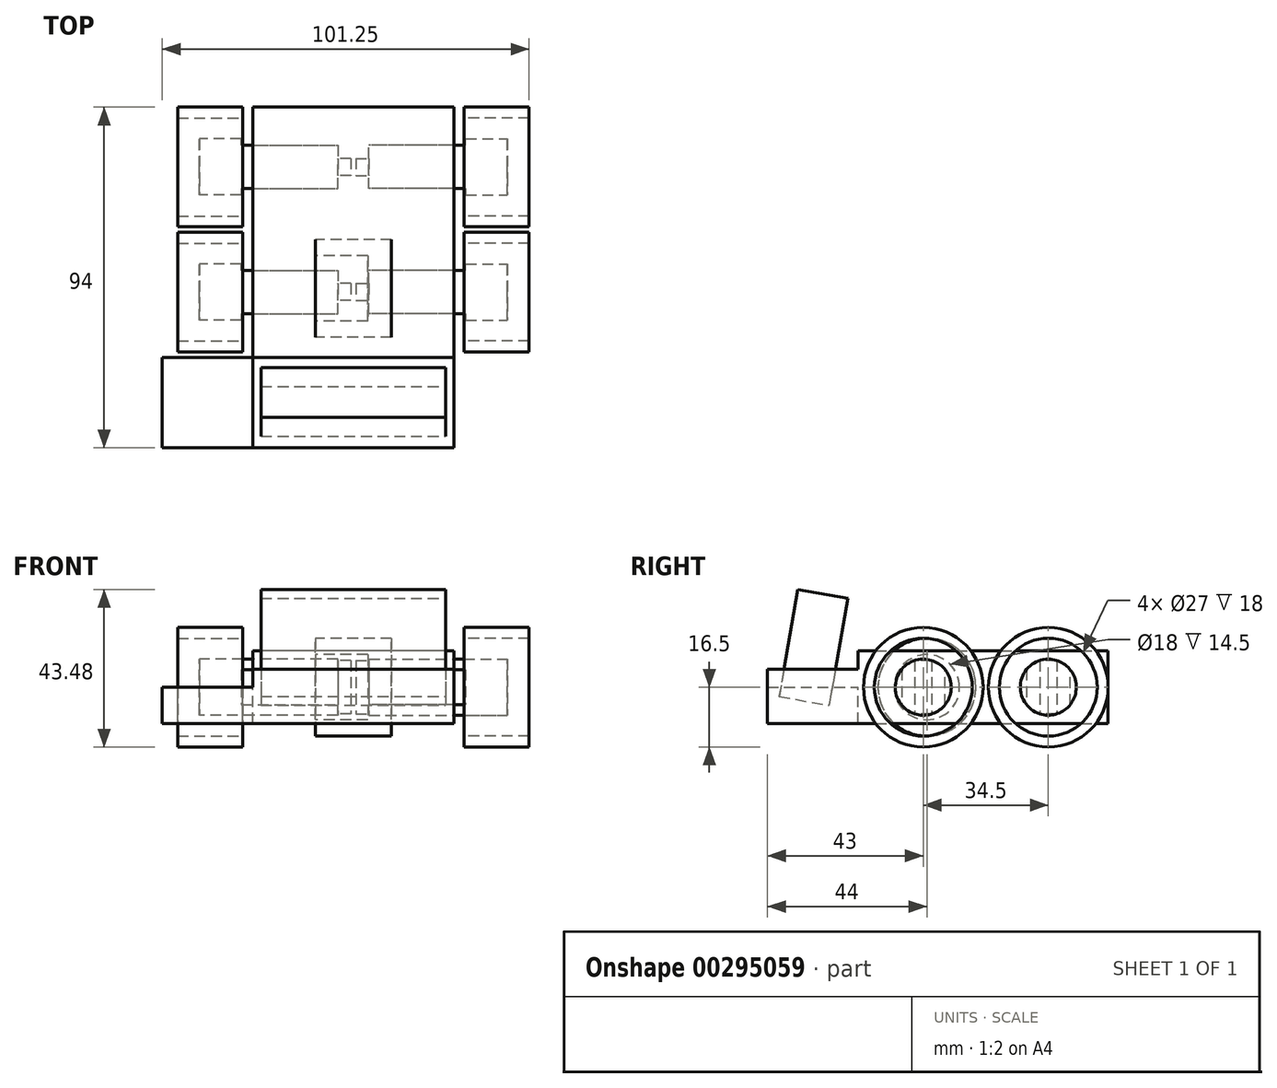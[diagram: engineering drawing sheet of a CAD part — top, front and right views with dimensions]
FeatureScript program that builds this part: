
annotation { "Feature Type Name" : "Feature", "Feature Type Description" : "" }
export const myFeature = defineFeature(function(context is Context, id is Id, definition is map)
    precondition{}
    {
        {
            assignVariable(context, id + "F0", {"name" : "GapMid", "anyValue" : 1.5 * mm});
        }
        {
            var Q0;
            Q0=qCreatedBy(makeId("Top.planeOp"),FACE);
            var sketch = newSketch(context, id + "F1", { "sketchPlane" : qUnion([Q0])});
            skLineSegment(sketch, "E0.bottom", {"start": v(-50, 50) * mm, "end": v(50, 50) * mm, "construction": true});
            skLineSegment(sketch, "E0.top", {"start": v(-50, -50) * mm, "end": v(50, -50) * mm, "construction": true});
            skLineSegment(sketch, "E0.left", {"start": v(-50, 50) * mm, "end": v(-50, -50) * mm, "construction": true});
            skLineSegment(sketch, "E0.right", {"start": v(50, 50) * mm, "end": v(50, -50) * mm, "construction": true});
            skLineSegment(sketch, "E1", {"start": v(0, 0) * mm, "end": v(39.5, 33.5) * mm, "construction": true});
            skSolve(sketch);
        }
        {
            var Q0;
            Q0=qCreatedBy(makeId("Right.planeOp"),FACE);
            var sketch = newSketch(context, id + "F2", { "sketchPlane" : qUnion([Q0])});
            skCircle(sketch, "E2", {"center": v(0, 0) * mm, "radius": 13.5 * mm});
            skCircle(sketch, "E3", {"center": v(0, 0) * mm, "radius": 16.5 * mm});
            skSolve(sketch);
        }
        {
            var Q0;
            Q0=makeQuery(id+"F2.imprint","IMPRINT",FACE,{"disambiguationData":[TD([[makeQuery(id+"F2.imprint","IMPRINT",EDGE,{"derivedFrom":sQuery(id+"F2.wireOp",EDGE,"E2")}),-1.0]])]});
            extrude(context, id + "F3", {"entities" : qUnion([Q0]), "endBound" : BoundingType.SYMMETRIC, "depth" : 18 * mm});
        }
        {
            var Q0;
            Q0=makeQuery(id+"F2.imprint","IMPRINT",FACE,{"disambiguationData":[TD([[makeQuery(id+"F2.imprint","IMPRINT",EDGE,{"derivedFrom":sQuery(id+"F2.wireOp",EDGE,"E2")}),1.0]])]});
            extrude(context, id + "F4", {"entities" : qUnion([Q0]), "endBound" : BoundingType.SYMMETRIC, "depth" : 21 * mm});
        }
        {
            var Q0;
            Q0=makeQuery(id+"F4.opExtrude","CAP_FACE",FACE,{"disambiguationData":[OSD([sQuery(id+"F2.wireOp",EDGE,"E2")])],"isStart":true});
            var sketch = newSketch(context, id + "F5", { "sketchPlane" : qUnion([Q0])});
            skCircle(sketch, "E4", {"center": v(0, 0) * mm, "radius": 9 * mm});
            skSolve(sketch);
        }
        {
            var Q0;
            Q0=makeQuery(id+"F5.imprint","IMPRINT",FACE,{"disambiguationData":[TD([[makeQuery(id+"F5.imprint","IMPRINT",EDGE,{"derivedFrom":sQuery(id+"F5.wireOp",EDGE,"E4")}),1.0]])]});
            var Q1;
            Q1=sQuery(id+"F5.wireOp",EDGE,"E4");
            extrude(context, id + "F6", {"entities" : qUnion([Q0]), "operationType" : NewBodyOperationType.REMOVE, "surfaceEntities" : qUnion([Q1]), "oppositeDirection" : true, "depth" : 14.5 * mm});
        }
        {
            var Q0;
            Q0=makeQuery(id+"F6.boolean.opBoolean","COPY",FACE,{"derivedFrom":makeQuery(id+"F6.opExtrude","CAP_FACE",FACE,{"disambiguationData":[OSD([sQuery(id+"F5.wireOp",EDGE,"E4")])],"isStart":false})});
            cPlane(context, id + "F7", {"entities" : qUnion([Q0]), "cplaneType" : CPlaneType.OFFSET, "offset" : 1 * mm, "width" : 150 * mm, "height" : 150 * mm});
        }
        {
            var Q0;
            Q0=qCreatedBy(id+"F7.planeOp",FACE);
            var sketch = newSketch(context, id + "F8", { "sketchPlane" : qUnion([Q0])});
            skCircle(sketch, "E5", {"center": v(0, 0) * mm, "radius": 7.73 * mm});
            skSolve(sketch);
        }
        {
            var Q0;
            Q0=makeQuery(id+"F8.imprint","IMPRINT",FACE,{"disambiguationData":[TD([[makeQuery(id+"F8.imprint","IMPRINT",EDGE,{"derivedFrom":sQuery(id+"F8.wireOp",EDGE,"E5")}),1.0]])]});
            extrude(context, id + "F9", {"entities" : qUnion([Q0]), "depth" : 38.22 * mm});
        }
        {
            var Q0;
            Q0=makeQuery(id+"F9.opExtrude","CAP_FACE",FACE,{"disambiguationData":[OSD([sQuery(id+"F8.wireOp",EDGE,"E5")])],"isStart":false});
            var sketch = newSketch(context, id + "F10", { "sketchPlane" : qUnion([Q0])});
            skLineSegment(sketch, "E6", {"start": v(-6, 0) * mm, "end": v(6, 0) * mm, "construction": true});
            skLineSegment(sketch, "E7", {"start": v(-6, -4.87) * mm, "end": v(-6, 4.87) * mm});
            skLineSegment(sketch, "E8", {"start": v(6, 4.87) * mm, "end": v(6, -4.87) * mm});
            skSolve(sketch);
        }
        {
            var Q0;
            {var subQ0=sQuery(id+"F10.wireOp",EDGE,"E7");Q0=makeQuery(id+"F10.imprint","IMPRINT",FACE,{"disambiguationData":[TD([[makeQuery(id+"F10.imprint","IMPRINT",EDGE,{"derivedFrom":subQ0}),1.0]])]});}
            var Q1;
            {var subQ0=sQuery(id+"F10.wireOp",EDGE,"E8");Q1=makeQuery(id+"F10.imprint","IMPRINT",FACE,{"disambiguationData":[TD([[makeQuery(id+"F10.imprint","IMPRINT",EDGE,{"derivedFrom":subQ0}),1.0]])]});}
            extrude(context, id + "F11", {"entities" : qUnion([Q0, Q1]), "operationType" : NewBodyOperationType.REMOVE, "oppositeDirection" : true, "depth" : 26.7 * mm});
        }
        {
            var Q0;
            Q0=makeQuery(id+"F9.opExtrude","CAP_FACE",FACE,{"disambiguationData":[OSD([sQuery(id+"F8.wireOp",EDGE,"E5")])],"isStart":false});
            var sketch = newSketch(context, id + "F12", { "sketchPlane" : qUnion([Q0])});
            skLineSegment(sketch, "E9", {"start": v(-2.35, 7.36) * mm, "end": v(2.35, 7.36) * mm});
            skLineSegment(sketch, "E10", {"start": v(-2.35, -7.36) * mm, "end": v(2.35, -7.36) * mm});
            skLineSegment(sketch, "E11", {"start": v(-2.35, 7.36) * mm, "end": v(-2.35, -7.36) * mm});
            skLineSegment(sketch, "E12", {"start": v(2.35, 7.36) * mm, "end": v(2.35, -7.36) * mm});
            skSolve(sketch);
        }
        {
            var Q0;
            Q0=makeQuery(id+"F12.imprint","IMPRINT",FACE,{"disambiguationData":[TD([[makeQuery(id+"F12.imprint","IMPRINT",EDGE,{"derivedFrom":sQuery(id+"F12.wireOp",EDGE,"E9")}),-1.0]])]});
            extrude(context, id + "F13", {"entities" : qUnion([Q0]), "operationType" : NewBodyOperationType.ADD, "depth" : 3.6 * mm});
        }
        {
            var Q0;
            Q0=makeQuery(id+"F3.opExtrude","SWEPT_BODY",BODY,{"disambiguationData":[OSD([sQuery(id+"F2.wireOp",EDGE,"E2"),sQuery(id+"F2.wireOp",EDGE,"E3")])]});
            var Q1;
            Q1=makeQuery(id+"F9.opExtrude","SWEPT_BODY",BODY,{"disambiguationData":[OSD([sQuery(id+"F8.wireOp",EDGE,"E5")])]});
            var Q2;
            Q2=sQuery(id+"F1.wireOp",EDGE,"E1");
            transform(context, id + "F14", {"entities" : qUnion([Q0, Q1]), "transformType" : TransformType.TRANSLATION_ENTITY, "oppositeDirectionEntity" : false, "transformLine" : qUnion([Q2]), "makeCopy" : false});
        }
        {
            var Q0;
            Q0=makeQuery(id+"F3.opExtrude","SWEPT_BODY",BODY,{"disambiguationData":[OSD([sQuery(id+"F2.wireOp",EDGE,"E2"),sQuery(id+"F2.wireOp",EDGE,"E3")])]});
            var Q1;
            Q1=makeQuery(id+"F9.opExtrude","SWEPT_BODY",BODY,{"disambiguationData":[OSD([sQuery(id+"F8.wireOp",EDGE,"E5")])]});
            var Q2;
            Q2=qCreatedBy(makeId("Right.planeOp"),FACE);
            mirror(context, id + "F15", {"entities" : qUnion([Q0, Q1]), "mirrorPlane" : qUnion([Q2])});
        }
        {
            var Q0;
            Q0=makeQuery(id+"F15.opPattern","COPY",BODY,{"derivedFrom":makeQuery(id+"F3.opExtrude","SWEPT_BODY",BODY,{"disambiguationData":[OSD([sQuery(id+"F2.wireOp",EDGE,"E2"),sQuery(id+"F2.wireOp",EDGE,"E3")])]}),"instanceName":"1"});
            var Q1;
            Q1=makeQuery(id+"F3.opExtrude","SWEPT_BODY",BODY,{"disambiguationData":[OSD([sQuery(id+"F2.wireOp",EDGE,"E2"),sQuery(id+"F2.wireOp",EDGE,"E3")])]});
            var Q2;
            Q2=makeQuery(id+"F9.opExtrude","SWEPT_BODY",BODY,{"disambiguationData":[OSD([sQuery(id+"F8.wireOp",EDGE,"E5")])]});
            var Q3;
            Q3=makeQuery(id+"F15.opPattern","COPY",BODY,{"derivedFrom":makeQuery(id+"F9.opExtrude","SWEPT_BODY",BODY,{"disambiguationData":[OSD([sQuery(id+"F8.wireOp",EDGE,"E5")])]}),"instanceName":"1"});
            var Q4;
            Q4=makeQuery(id+"F15.opPattern","COPY",FACE,{"derivedFrom":makeQuery(id+"F11.boolean.opBoolean","COPY",FACE,{"derivedFrom":makeQuery(id+"F11.opExtrude","SWEPT_FACE",FACE,{"disambiguationData":[OSD([sQuery(id+"F10.wireOp",EDGE,"E8")])]})}),"instanceName":"1"});
            transform(context, id + "F16", {"entities" : qUnion([Q0, Q1, Q2, Q3]), "transformType" : TransformType.TRANSLATION_DISTANCE, "transformDirection" : qUnion([Q4]), "distance" : getVariable(context, 'GapMid') + 33 * mm, "makeCopy" : true});
        }
        {
            var Q0;
            Q0=makeQuery(id+"F16.opPattern","COPY",FACE,{"derivedFrom":makeQuery(id+"F15.opPattern","COPY",FACE,{"derivedFrom":makeQuery(id+"F4.opExtrude","CAP_FACE",FACE,{"disambiguationData":[OSD([sQuery(id+"F2.wireOp",EDGE,"E2")])],"isStart":false}),"instanceName":"1"}),"instanceName":"1"});
            var sketch = newSketch(context, id + "F17", { "sketchPlane" : qUnion([Q0])});
            skPoint(sketch, "E13", {"position": v(1, 0) * mm});
            skLineSegment(sketch, "E14", {"start": v(1, -5.4) * mm, "end": v(1, 5.4) * mm});
            skSolve(sketch);
        }
        {
            var Q0;
            Q0=qCreatedBy(makeId("Top.planeOp"),FACE);
            var sketch = newSketch(context, id + "F18", { "sketchPlane" : qUnion([Q0])});
            skLineSegment(sketch, "E15.bottom", {"start": v(27.75, -19) * mm, "end": v(-27.75, -19) * mm});
            skLineSegment(sketch, "E15.top", {"start": v(27.75, 50) * mm, "end": v(-27.75, 50) * mm});
            skLineSegment(sketch, "E15.left", {"start": v(27.75, -19) * mm, "end": v(27.75, 50) * mm});
            skLineSegment(sketch, "E15.right", {"start": v(-27.75, -19) * mm, "end": v(-27.75, 50) * mm});
            skSolve(sketch);
        }
        {
            var Q0;
            Q0=makeQuery(id+"F18.imprint","IMPRINT",FACE,{"disambiguationData":[TD([[makeQuery(id+"F18.imprint","IMPRINT",EDGE,{"derivedFrom":sQuery(id+"F18.wireOp",EDGE,"E15.bottom")}),-1.0]])]});
            extrude(context, id + "F19", {"entities" : qUnion([Q0]), "oppositeDirection" : true, "depth" : 10 * mm});
        }
        {
            var Q0;
            Q0=makeQuery(id+"F18.imprint","IMPRINT",FACE,{"disambiguationData":[TD([[makeQuery(id+"F18.imprint","IMPRINT",EDGE,{"derivedFrom":sQuery(id+"F18.wireOp",EDGE,"E15.bottom")}),-1.0]])]});
            var sketch = newSketch(context, id + "F20", { "sketchPlane" : qUnion([Q0])});
            skLineSegment(sketch, "E16.bottom", {"start": v(-25.5, 15) * mm, "end": v(25.5, 15) * mm});
            skLineSegment(sketch, "E16.top", {"start": v(-25.5, -15) * mm, "end": v(25.5, -15) * mm});
            skLineSegment(sketch, "E16.left", {"start": v(-25.5, 15) * mm, "end": v(-25.5, -15) * mm});
            skLineSegment(sketch, "E16.right", {"start": v(25.5, 15) * mm, "end": v(25.5, -15) * mm});
            skLineSegment(sketch, "E17", {"start": v(0, -15) * mm, "end": v(0, 15) * mm, "construction": true});
            skSolve(sketch);
        }
        {
            var Q0;
            Q0 = qSketchRegion(id + "F20", true);
            extrude(context, id + "F21", {"entities" : qUnion([Q0]), "depth" : 14 * mm});
        }
        {
            var Q0;
            Q0=makeQuery(id+"F21.opExtrude","SWEPT_BODY",BODY,{"disambiguationData":[OSD([sQuery(id+"F20.wireOp",EDGE,"E16.bottom"),sQuery(id+"F20.wireOp",EDGE,"E16.top"),sQuery(id+"F20.wireOp",EDGE,"E16.left"),sQuery(id+"F20.wireOp",EDGE,"E16.right")])]});
            var Q1;
            Q1=makeQuery(id+"F21.opExtrude","CAP_EDGE",EDGE,{"disambiguationData":[OSD([sQuery(id+"F20.wireOp",EDGE,"E16.top")])],"isStart":true});
            transform(context, id + "F22", {"entities" : qUnion([Q0]), "transformType" : TransformType.ROTATION, "transformAxis" : qUnion([Q1]), "angle" : 80 * degree, "makeCopy" : false});
        }
        {
            var Q0;
            Q0=makeQuery(id+"F21.opExtrude","SWEPT_BODY",BODY,{"disambiguationData":[OSD([sQuery(id+"F20.wireOp",EDGE,"E16.bottom"),sQuery(id+"F20.wireOp",EDGE,"E16.top"),sQuery(id+"F20.wireOp",EDGE,"E16.left"),sQuery(id+"F20.wireOp",EDGE,"E16.right")])]});
            transform(context, id + "F23", {"entities" : qUnion([Q0]), "transformType" : TransformType.TRANSLATION_3D, "dx" : 0 * mm, "dy" : -12 * mm, "dz" : -5 * mm, "makeCopy" : false});
        }
        {
            var Q0;
            Q0=makeQuery(id+"F19.opExtrude","CAP_FACE",FACE,{"disambiguationData":[OSD([sQuery(id+"F18.wireOp",EDGE,"E15.bottom"),sQuery(id+"F18.wireOp",EDGE,"E15.top"),sQuery(id+"F18.wireOp",EDGE,"E15.left"),sQuery(id+"F18.wireOp",EDGE,"E15.right")])],"isStart":true});
            extrude(context, id + "F24", {"entities" : qUnion([Q0]), "depth" : 10 * mm});
        }
        {
            var Q0;
            Q0=makeQuery(id+"F19.opExtrude","SWEPT_FACE",FACE,{"disambiguationData":[OSD([sQuery(id+"F18.wireOp",EDGE,"E15.bottom")])]});
            extrude(context, id + "F25", {"entities" : qUnion([Q0]), "depth" : 25 * mm});
        }
        {
            var Q0;
            {var subQ0=sQuery(id+"F18.wireOp",EDGE,"E15.bottom");Q0=makeQuery(id+"F25.opExtrude","SWEPT_FACE",FACE,{"disambiguationData":[OSD([subQ0]),TDD([makeQuery(id+"F19.opExtrude","CAP_EDGE",EDGE,{"disambiguationData":[OSD([subQ0])],"isStart":true})])]});}
            extrude(context, id + "F26", {"entities" : qUnion([Q0]), "depth" : 5 * mm});
        }
        {
            var Q0;
            Q0=makeQuery(id+"F25.opExtrude","SWEPT_FACE",FACE,{"disambiguationData":[OSD([sQuery(id+"F18.wireOp",EDGE,"E15.bottom"),sQuery(id+"F18.wireOp",EDGE,"E15.right")])]});
            extrude(context, id + "F27", {"entities" : qUnion([Q0]), "operationType" : NewBodyOperationType.ADD, "depth" : 25 * mm});
        }
    });
